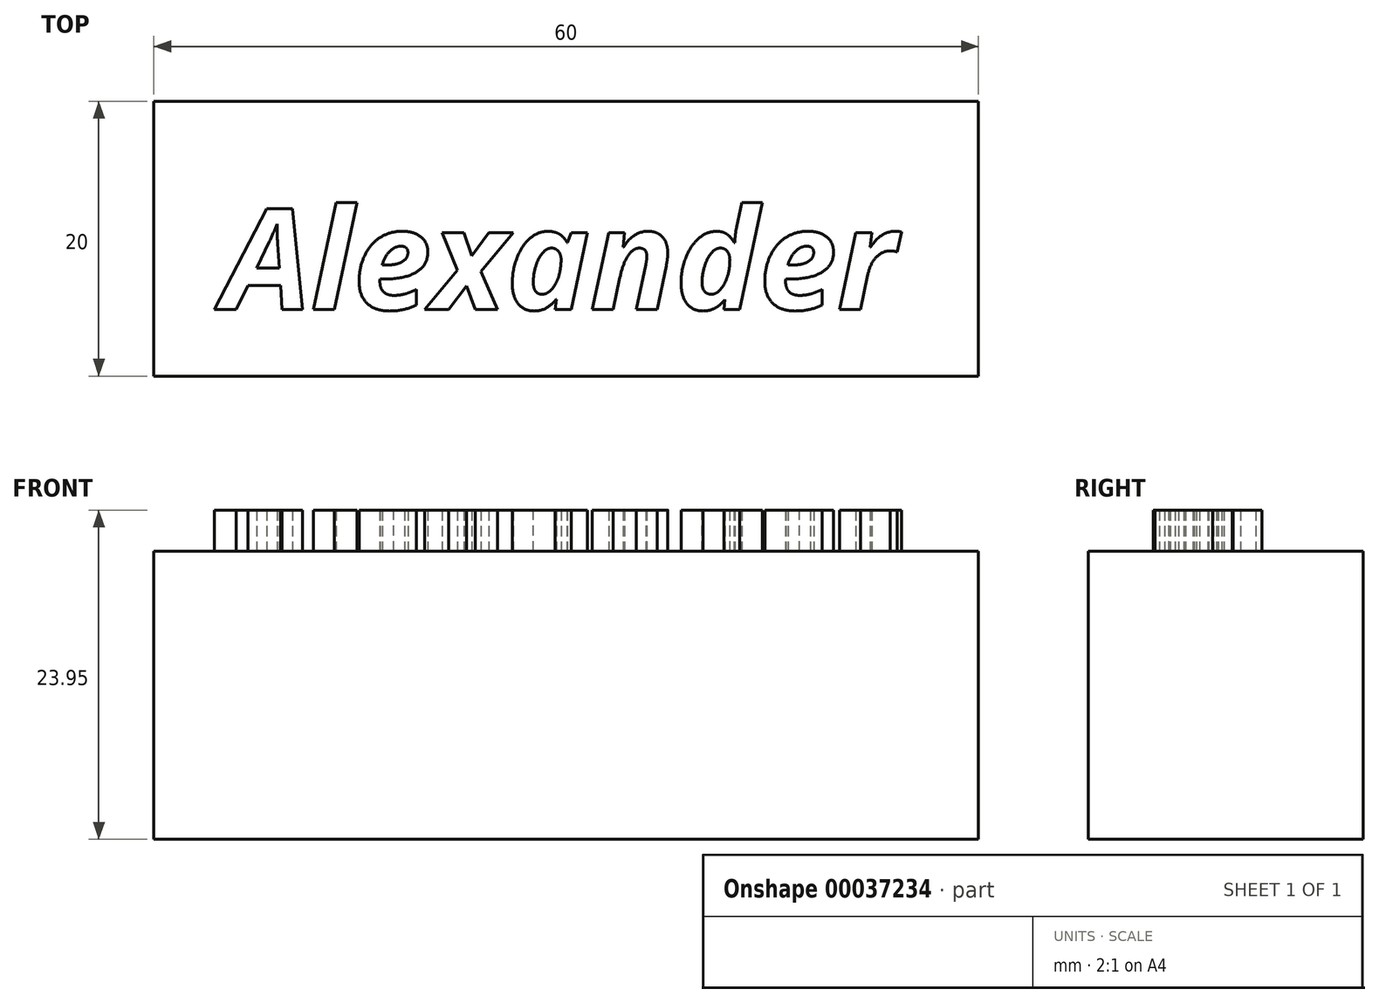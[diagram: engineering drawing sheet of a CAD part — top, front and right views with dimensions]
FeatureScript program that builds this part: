
annotation { "Feature Type Name" : "Feature", "Feature Type Description" : "" }
export const myFeature = defineFeature(function(context is Context, id is Id, definition is map)
    precondition{}
    {
        {
            var Q0;
            Q0=qCreatedBy(makeId("Top.planeOp"),FACE);
            var sketch = newSketch(context, id + "F0", { "sketchPlane" : qUnion([Q0])});
            skLineSegment(sketch, "E0.rect.bottom", {"start": v(30, 10) * mm, "end": v(-30, 10) * mm});
            skLineSegment(sketch, "E0.rect.top", {"start": v(30, -10) * mm, "end": v(-30, -10) * mm});
            skLineSegment(sketch, "E0.rect.left", {"start": v(30, 10) * mm, "end": v(30, -10) * mm});
            skLineSegment(sketch, "E0.rect.right", {"start": v(-30, 10) * mm, "end": v(-30, -10) * mm});
            skPoint(sketch, "E0.rect.middle", {"position": v(0, 0) * mm});
            skSolve(sketch);
        }
        {
            var Q0;
            Q0=makeQuery(id+"F0.imprint","IMPRINT",FACE,{"disambiguationData":[TD([[makeQuery(id+"F0.imprint","IMPRINT",EDGE,{"derivedFrom":sQuery(id+"F0.wireOp",EDGE,"E0.rect.bottom")}),1.0]])]});
            extrude(context, id + "F1", {"entities" : qUnion([Q0]), "depth" : 20.95 * mm});
        }
        {
            var Q0;
            Q0=makeQuery(id+"F1.opExtrude","CAP_FACE",FACE,{"disambiguationData":[OSD([sQuery(id+"F0.wireOp",EDGE,"E0.rect.bottom"),sQuery(id+"F0.wireOp",EDGE,"E0.rect.top"),sQuery(id+"F0.wireOp",EDGE,"E0.rect.left"),sQuery(id+"F0.wireOp",EDGE,"E0.rect.right")])],"isStart":false});
            var sketch = newSketch(context, id + "F2", { "sketchPlane" : qUnion([Q0])});
            skText(sketch, "E1", { "text": "Alexander", "fontName": "OpenSans-BoldItalic.ttf"});
            const initialGuessF2  = {"E1": [-0.025, -0.00516, 1, 0, 0.00738]};
            skSetInitialGuess(sketch, initialGuessF2);
            skSolve(sketch);
        }
        {
            var Q0;
            Q0 = qSketchRegion(id + "F2", true);
            extrude(context, id + "F3", {"entities" : qUnion([Q0]), "operationType" : NewBodyOperationType.ADD, "depth" : 3 * mm});
        }
    });
